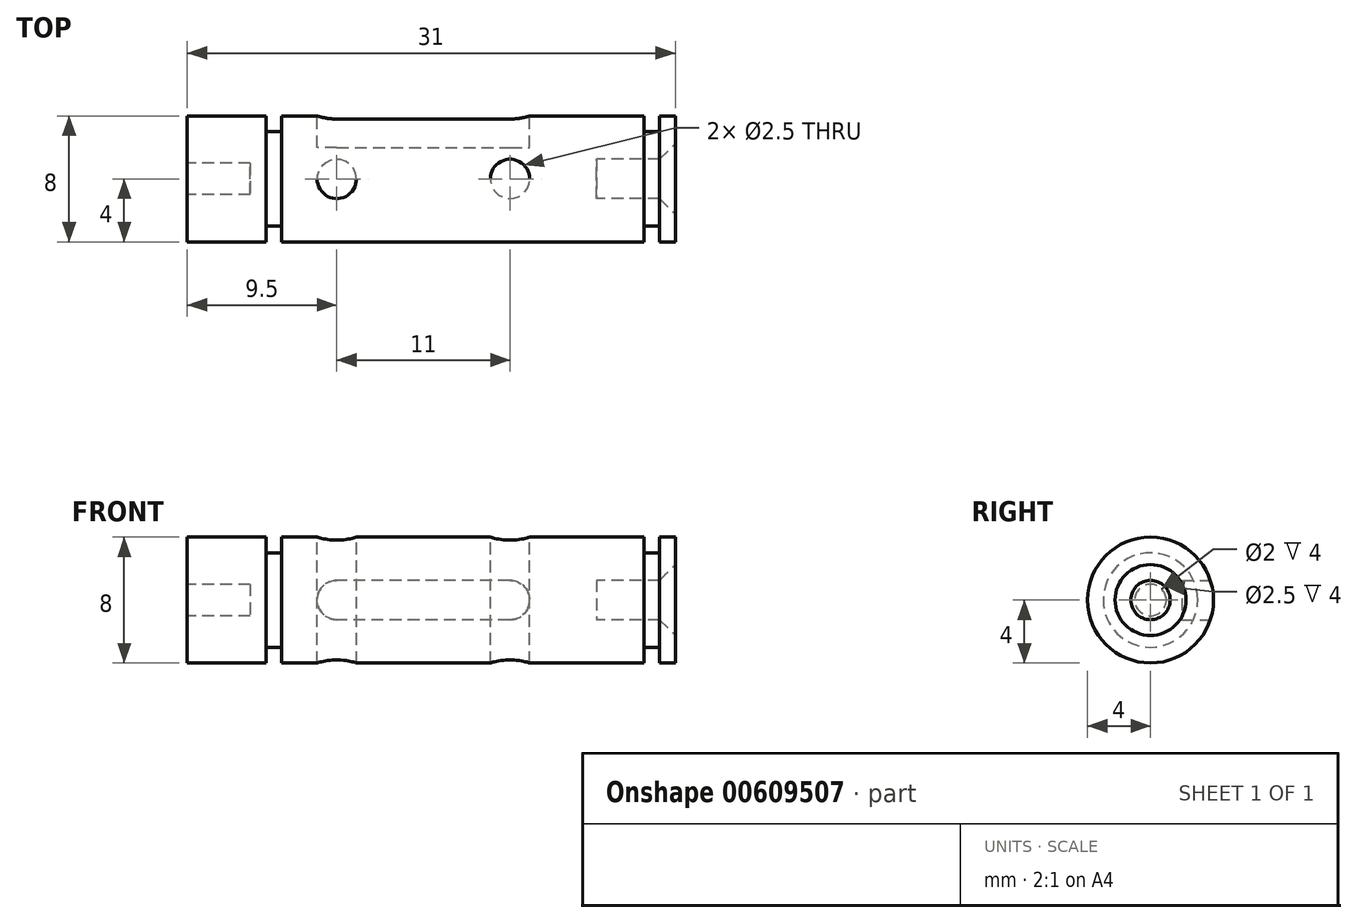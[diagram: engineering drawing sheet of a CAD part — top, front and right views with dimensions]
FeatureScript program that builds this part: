
annotation { "Feature Type Name" : "Feature", "Feature Type Description" : "" }
export const myFeature = defineFeature(function(context is Context, id is Id, definition is map)
    precondition{}
    {
        {
            var Q0;
            Q0=qCreatedBy(makeId("Top.planeOp"),FACE);
            var sketch = newSketch(context, id + "F0", { "sketchPlane" : qUnion([Q0])});
            skLineSegment(sketch, "E0", {"start": v(0, 2.97) * mm, "end": v(0, 4) * mm});
            skLineSegment(sketch, "E1", {"start": v(0, 4) * mm, "end": v(-1, 4) * mm});
            skLineSegment(sketch, "E2", {"start": v(-1, 4) * mm, "end": v(-1, 3) * mm});
            skLineSegment(sketch, "E3", {"start": v(-1, 3) * mm, "end": v(-2, 3) * mm});
            skLineSegment(sketch, "E4", {"start": v(-2, 3) * mm, "end": v(-2, 4) * mm});
            skLineSegment(sketch, "E5", {"start": v(-2, 4) * mm, "end": v(-3, 4) * mm});
            skLineSegment(sketch, "E6", {"start": v(-3, 4) * mm, "end": v(-8, 4) * mm});
            skLineSegment(sketch, "E7", {"start": v(-8, 4) * mm, "end": v(-8, 4) * mm});
            skLineSegment(sketch, "E8", {"start": v(-8, 4) * mm, "end": v(-13, 4) * mm});
            skLineSegment(sketch, "E9", {"start": v(-13, 4) * mm, "end": v(-13, 4) * mm});
            skLineSegment(sketch, "E10", {"start": v(-13, 4) * mm, "end": v(-19, 4) * mm});
            skLineSegment(sketch, "E11", {"start": v(-19, 4) * mm, "end": v(-19, 4) * mm});
            skLineSegment(sketch, "E12", {"start": v(-19, 4) * mm, "end": v(-24, 4) * mm});
            skLineSegment(sketch, "E13", {"start": v(-24, 4) * mm, "end": v(-24, 4) * mm});
            skLineSegment(sketch, "E14", {"start": v(-24, 4) * mm, "end": v(-25, 4) * mm});
            skLineSegment(sketch, "E15", {"start": v(-25, 4) * mm, "end": v(-25, 3) * mm});
            skLineSegment(sketch, "E16", {"start": v(-25, 3) * mm, "end": v(-26, 3) * mm});
            skLineSegment(sketch, "E17", {"start": v(-26, 3) * mm, "end": v(-26, 4) * mm});
            skLineSegment(sketch, "E18", {"start": v(-26, 4) * mm, "end": v(-31, 4) * mm});
            skLineSegment(sketch, "E19", {"start": v(-31, 4) * mm, "end": v(-31, 1) * mm});
            skLineSegment(sketch, "E20", {"start": v(-31, 1) * mm, "end": v(-27, 1) * mm});
            skLineSegment(sketch, "E21", {"start": v(-27, 1) * mm, "end": v(-27, 0) * mm});
            skLineSegment(sketch, "E22", {"start": v(0, 0) * mm, "end": v(11, 0) * mm, "construction": true});
            skLineSegment(sketch, "E23", {"start": v(-5, 0) * mm, "end": v(-27, 0) * mm});
            skPoint(sketch, "E24", {"position": v(-5.5, 4) * mm});
            skPoint(sketch, "E25", {"position": v(-16, 4) * mm});
            skPoint(sketch, "E26", {"position": v(-10.5, 4) * mm});
            skPoint(sketch, "E27", {"position": v(-21.5, 4) * mm});
            skLineSegment(sketch, "E28", {"start": v(-5, 0) * mm, "end": v(-5, 1.25) * mm});
            skLineSegment(sketch, "E29", {"start": v(-5, 1.25) * mm, "end": v(-1, 1.25) * mm});
            skLineSegment(sketch, "E30", {"start": v(-1, 1.25) * mm, "end": v(0, 1.25) * mm});
            skLineSegment(sketch, "E31", {"start": v(0, 1.25) * mm, "end": v(0, 2.97) * mm});
            skSolve(sketch);
        }
        {
            var Q0;
            Q0=makeQuery(id+"F0.imprint","IMPRINT",FACE,{"disambiguationData":[TD([[makeQuery(id+"F0.imprint","IMPRINT",EDGE,{"derivedFrom":sQuery(id+"F0.wireOp",EDGE,"E0")}),1.0]])]});
            var Q1;
            Q1=sQuery(id+"F0.wireOp",EDGE,"E22");
            revolve(context, id + "F1", {"entities" : qUnion([Q0]), "axis" : qUnion([Q1]), "revolveType" : RevolveType.FULL});
        }
        {
            var Q0;
            Q0=qCreatedBy(makeId("Top.planeOp"),FACE);
            cPlane(context, id + "F2", {"entities" : qUnion([Q0]), "cplaneType" : CPlaneType.OFFSET, "offset" : 4 * mm, "width" : 150 * mm, "height" : 150 * mm});
        }
        {
            var Q0;
            Q0=qCreatedBy(id+"F2.planeOp",FACE);
            var sketch = newSketch(context, id + "F3", { "sketchPlane" : qUnion([Q0])});
            skCircle(sketch, "E32", {"center": v(-10.5, 0) * mm, "radius": 1.25 * mm});
            skCircle(sketch, "E33", {"center": v(-21.5, 0) * mm, "radius": 1.25 * mm});
            skSolve(sketch);
        }
        {
            var Q0;
            Q0=makeQuery(id+"F3.imprint","IMPRINT",FACE,{"disambiguationData":[TD([[makeQuery(id+"F3.imprint","IMPRINT",EDGE,{"derivedFrom":sQuery(id+"F3.wireOp",EDGE,"E33")}),1.0]])]});
            var Q1;
            Q1=makeQuery(id+"F3.imprint","IMPRINT",FACE,{"disambiguationData":[TD([[makeQuery(id+"F3.imprint","IMPRINT",EDGE,{"derivedFrom":sQuery(id+"F3.wireOp",EDGE,"E32")}),1.0]])]});
            extrude(context, id + "F4", {"entities" : qUnion([Q0, Q1]), "operationType" : NewBodyOperationType.REMOVE, "oppositeDirection" : true, "depth" : 25 * mm, "offsetDistance" : 25 * mm});
        }
        {
            var Q0;
            Q0=makeQuery(id+"F1.opRevolve","SWEPT_EDGE",EDGE,{"disambiguationData":[OSD([sQuery(id+"F0.wireOp",EDGE,"E30"),sQuery(id+"F0.wireOp",EDGE,"E31")])]});
            var Q1;
            Q1=makeQuery(id+"FymvyWvEsBwVXzy_2.opExtrude","CAP_EDGE",EDGE,{"disambiguationData":[OSD([sQuery(id+"F0.wireOp",EDGE,"E30"),sQuery(id+"F0.wireOp",EDGE,"E31")])],"isStart":false});
            chamfer(context, id + "F5", {"entities" : qUnion([Q0, Q1]), "width" : 1 * mm, "tangentPropagation" : true});
        }
        {
            var Q0;
            Q0=qCreatedBy(makeId("Front.planeOp"),FACE);
            cPlane(context, id + "F6", {"entities" : qUnion([Q0]), "cplaneType" : CPlaneType.OFFSET, "offset" : 4 * mm, "oppositeDirection" : true, "width" : 150 * mm, "height" : 150 * mm});
        }
        {
            var Q0;
            Q0=qCreatedBy(id+"F6.planeOp",FACE);
            var sketch = newSketch(context, id + "F7", { "sketchPlane" : qUnion([Q0])});
            skArc(sketch, "E34", {"start": v(-10.5, -1.25) * mm, "mid": v(-9.25, 0) * mm, "end": v(-10.5, 1.25) * mm});
            skArc(sketch, "E35", {"start": v(-21.5, 1.25) * mm, "mid": v(-22.75, 0) * mm, "end": v(-21.5, -1.25) * mm});
            skLineSegment(sketch, "E36", {"start": v(-21.5, 1.25) * mm, "end": v(-10.5, 1.25) * mm});
            skLineSegment(sketch, "E37", {"start": v(-21.5, -1.25) * mm, "end": v(-10.5, -1.25) * mm});
            skSolve(sketch);
        }
        {
            var Q0;
            Q0=makeQuery(id+"F7.imprint","IMPRINT",FACE,{"disambiguationData":[TD([[makeQuery(id+"F7.imprint","IMPRINT",EDGE,{"derivedFrom":sQuery(id+"F7.wireOp",EDGE,"E34")}),1.0]])]});
            extrude(context, id + "F8", {"entities" : qUnion([Q0]), "operationType" : NewBodyOperationType.REMOVE, "depth" : 2 * mm, "offsetDistance" : 25 * mm});
        }
    });
